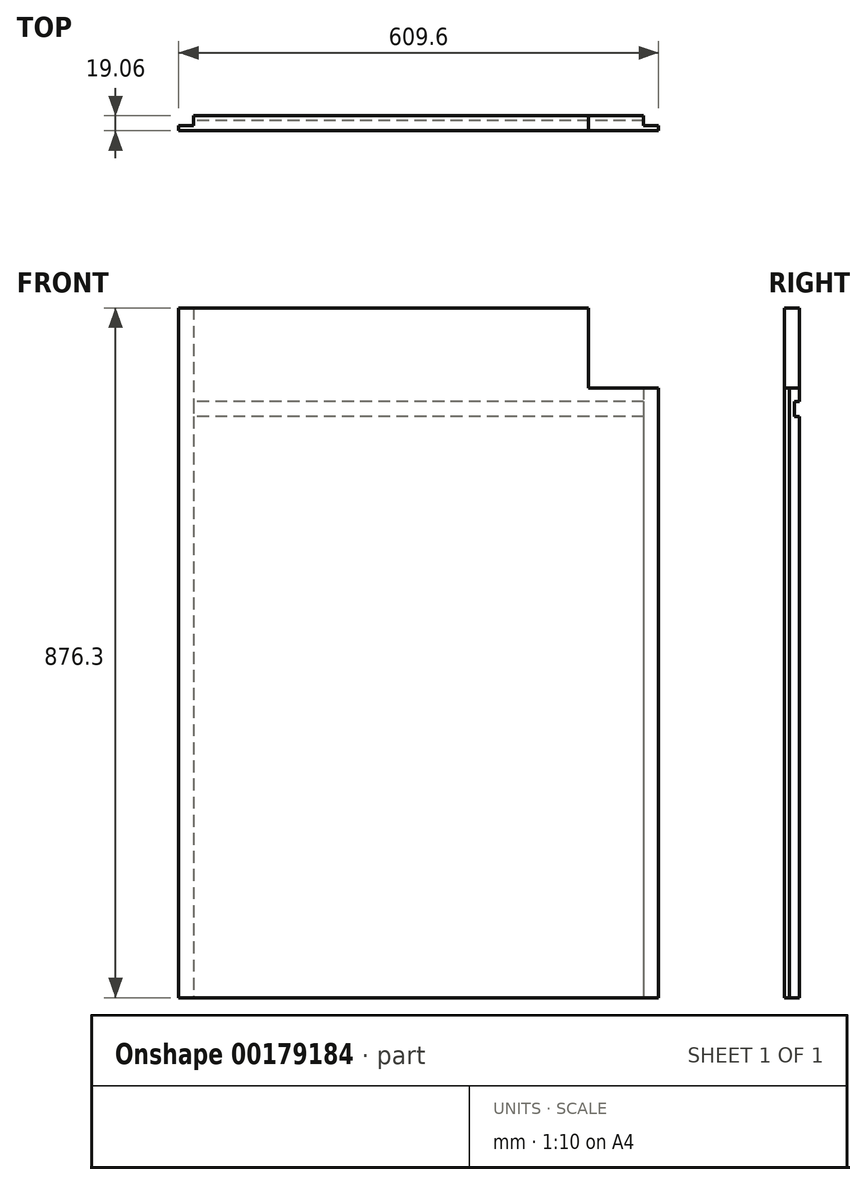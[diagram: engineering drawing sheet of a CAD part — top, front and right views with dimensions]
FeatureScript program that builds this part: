
annotation { "Feature Type Name" : "Feature", "Feature Type Description" : "" }
export const myFeature = defineFeature(function(context is Context, id is Id, definition is map)
    precondition{}
    {
        {
            var Q0;
            Q0=qCreatedBy(makeId("Front.planeOp"),FACE);
            var sketch = newSketch(context, id + "F0", { "sketchPlane" : qUnion([Q0])});
            skLineSegment(sketch, "E0.bottom", {"start": v(-247.9, 438.15) * mm, "end": v(361.7, 438.15) * mm});
            skLineSegment(sketch, "E0.top", {"start": v(-247.9, -438.15) * mm, "end": v(361.7, -438.15) * mm});
            skLineSegment(sketch, "E0.left", {"start": v(-247.9, 438.15) * mm, "end": v(-247.9, -438.15) * mm});
            skLineSegment(sketch, "E0.right", {"start": v(361.7, 438.15) * mm, "end": v(361.7, -438.15) * mm});
            skLineSegment(sketch, "E1", {"start": v(-247.9, 0) * mm, "end": v(361.7, 0) * mm});
            skSolve(sketch);
        }
        {
            var Q0;
            {var subQ0=sQuery(id+"F0.wireOp",EDGE,"E0.bottom");Q0=makeQuery(id+"F0.imprint","IMPRINT",FACE,{"disambiguationData":[TD([[makeQuery(id+"F0.imprint","IMPRINT",EDGE,{"derivedFrom":subQ0}),-1.0]])]});}
            var Q1;
            {var subQ0=sQuery(id+"F0.wireOp",EDGE,"E0.top");Q1=makeQuery(id+"F0.imprint","IMPRINT",FACE,{"disambiguationData":[TD([[makeQuery(id+"F0.imprint","IMPRINT",EDGE,{"derivedFrom":subQ0}),1.0]])]});}
            extrude(context, id + "F1", {"entities" : qUnion([Q0, Q1]), "depth" : 19.05 * mm, "symmetric" : true});
        }
        {
            var Q0;
            Q0=makeQuery(id+"F1.opExtrude","CAP_FACE",FACE,{"disambiguationData":[OSD([sQuery(id+"F0.wireOp",EDGE,"E0.bottom"),sQuery(id+"F0.wireOp",EDGE,"E0.top"),sQuery(id+"F0.wireOp",EDGE,"E0.left"),sQuery(id+"F0.wireOp",EDGE,"E0.right")])],"isStart":true});
            var sketch = newSketch(context, id + "F2", { "sketchPlane" : qUnion([Q0])});
            skLineSegment(sketch, "E2.bottom", {"start": v(-361.7, 438.15) * mm, "end": v(-342.65, 438.15) * mm});
            skLineSegment(sketch, "E2.top", {"start": v(-361.7, -438.15) * mm, "end": v(-342.65, -438.15) * mm});
            skLineSegment(sketch, "E2.left", {"start": v(-361.7, 438.15) * mm, "end": v(-361.7, -438.15) * mm});
            skLineSegment(sketch, "E2.right", {"start": v(-342.65, 438.15) * mm, "end": v(-342.65, -438.15) * mm});
            skLineSegment(sketch, "E3.bottom", {"start": v(247.9, 438.15) * mm, "end": v(228.85, 438.15) * mm});
            skLineSegment(sketch, "E3.top", {"start": v(247.9, -438.15) * mm, "end": v(228.85, -438.15) * mm});
            skLineSegment(sketch, "E3.left", {"start": v(247.9, 438.15) * mm, "end": v(247.9, -438.15) * mm});
            skLineSegment(sketch, "E3.right", {"start": v(228.85, 438.15) * mm, "end": v(228.85, -438.15) * mm});
            skSolve(sketch);
        }
        {
            var Q0;
            Q0=qSketchRegion(id+"F2",true);
            extrude(context, id + "F3", {"entities" : qUnion([Q0]), "operationType" : NewBodyOperationType.REMOVE, "oppositeDirection" : true, "depth" : 12.7 * mm});
        }
        {
            var Q0;
            Q0=makeQuery(id+"F1.opExtrude","CAP_FACE",FACE,{"disambiguationData":[OSD([sQuery(id+"F0.wireOp",EDGE,"E0.bottom"),sQuery(id+"F0.wireOp",EDGE,"E0.top"),sQuery(id+"F0.wireOp",EDGE,"E0.left"),sQuery(id+"F0.wireOp",EDGE,"E0.right")])],"isStart":true});
            var sketch = newSketch(context, id + "F4", { "sketchPlane" : qUnion([Q0])});
            skLineSegment(sketch, "E4.bottom", {"start": v(-342.65, 300.04) * mm, "end": v(228.85, 300.04) * mm});
            skLineSegment(sketch, "E4.top", {"start": v(-342.65, 319.09) * mm, "end": v(228.85, 319.09) * mm});
            skLineSegment(sketch, "E4.left", {"start": v(-342.65, 300.04) * mm, "end": v(-342.65, 319.09) * mm});
            skLineSegment(sketch, "E4.right", {"start": v(228.85, 300.04) * mm, "end": v(228.85, 319.09) * mm});
            skSolve(sketch);
        }
        {
            var Q0;
            Q0=makeQuery(id+"F4.imprint","IMPRINT",FACE,{"disambiguationData":[TD([[makeQuery(id+"F4.imprint","IMPRINT",EDGE,{"derivedFrom":sQuery(id+"F4.wireOp",EDGE,"E4.bottom")}),1.0]])]});
            extrude(context, id + "F5", {"entities" : qUnion([Q0]), "operationType" : NewBodyOperationType.REMOVE, "oppositeDirection" : true, "depth" : 6.35 * mm});
        }
        {
            var Q0;
            Q0=makeQuery(id+"F1.opExtrude","CAP_FACE",FACE,{"disambiguationData":[OSD([sQuery(id+"F0.wireOp",EDGE,"E0.bottom"),sQuery(id+"F0.wireOp",EDGE,"E0.top"),sQuery(id+"F0.wireOp",EDGE,"E0.left"),sQuery(id+"F0.wireOp",EDGE,"E0.right")])],"isStart":false});
            var sketch = newSketch(context, id + "F6", { "sketchPlane" : qUnion([Q0])});
            skLineSegment(sketch, "E5.bottom", {"start": v(361.7, 438.15) * mm, "end": v(272.8, 438.15) * mm});
            skLineSegment(sketch, "E5.top", {"start": v(361.7, 336.55) * mm, "end": v(272.8, 336.55) * mm});
            skLineSegment(sketch, "E5.left", {"start": v(361.7, 438.15) * mm, "end": v(361.7, 336.55) * mm});
            skLineSegment(sketch, "E5.right", {"start": v(272.8, 438.15) * mm, "end": v(272.8, 336.55) * mm});
            skSolve(sketch);
        }
        {
            var Q0;
            Q0=makeQuery(id+"F6.imprint","IMPRINT",FACE,{"disambiguationData":[TD([[makeQuery(id+"F6.imprint","IMPRINT",EDGE,{"derivedFrom":sQuery(id+"F6.wireOp",EDGE,"E5.bottom")}),-1.0]])]});
            extrude(context, id + "F7", {"entities" : qUnion([Q0]), "operationType" : NewBodyOperationType.REMOVE, "endBound" : BoundingType.THROUGH_ALL, "oppositeDirection" : true, "depth" : 25.4 * mm});
        }
    });
